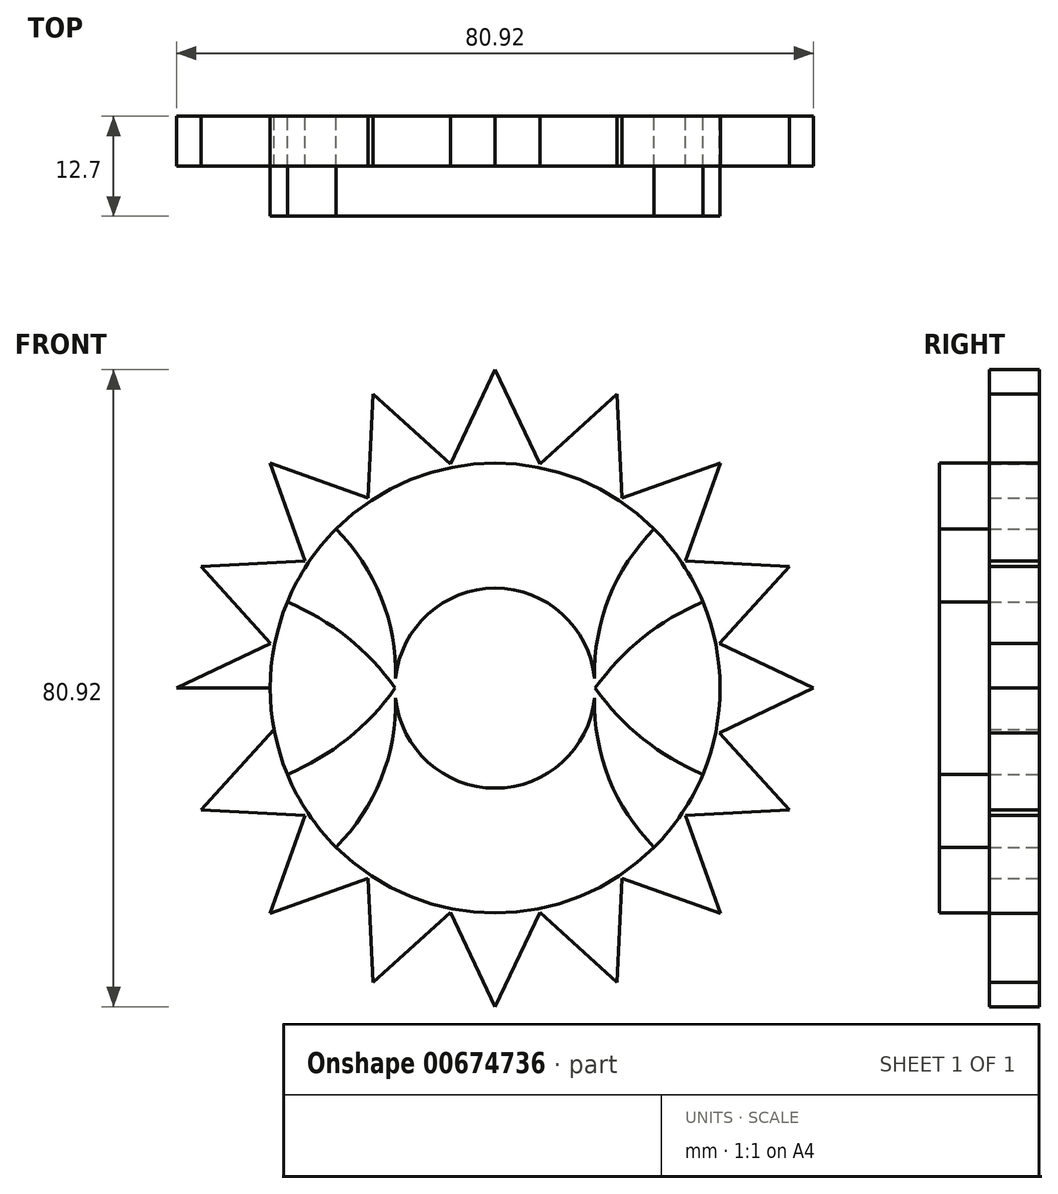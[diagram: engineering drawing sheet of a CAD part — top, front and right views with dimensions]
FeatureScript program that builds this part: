
annotation { "Feature Type Name" : "Feature", "Feature Type Description" : "" }
export const myFeature = defineFeature(function(context is Context, id is Id, definition is map)
    precondition{}
    {
        {
            var Q0;
            Q0=qCreatedBy(makeId("Front.planeOp"),FACE);
            var sketch = newSketch(context, id + "F0", { "sketchPlane" : qUnion([Q0])});
            skCircle(sketch, "E0", {"center": v(0, 0) * mm, "radius": 12.7 * mm});
            skCircle(sketch, "E1", {"center": v(0, 0) * mm, "radius": 28.58 * mm});
            skLineSegment(sketch, "E2", {"start": v(0, 28.58) * mm, "end": v(0, 40.46) * mm});
            skLineSegment(sketch, "E3", {"start": v(0, 40.46) * mm, "end": v(-5.93, 27.95) * mm});
            skLineSegment(sketch, "E4.MirrorCS", {"start": v(0, 40.46) * mm, "end": v(5.93, 27.95) * mm});
            skLineSegment(sketch, "E5.1.0", {"start": v(-15.48, 37.38) * mm, "end": v(-16.17, 23.56) * mm});
            skLineSegment(sketch, "E5.1.1", {"start": v(-15.48, 37.38) * mm, "end": v(-5.22, 28.1) * mm});
            skLineSegment(sketch, "E5.1.2", {"start": v(-10.94, 26.4) * mm, "end": v(-15.48, 37.38) * mm});
            skLineSegment(sketch, "E5.2.0", {"start": v(-28.6, 28.6) * mm, "end": v(-23.96, 15.57) * mm});
            skLineSegment(sketch, "E5.2.1", {"start": v(-28.6, 28.6) * mm, "end": v(-15.57, 23.96) * mm});
            skLineSegment(sketch, "E5.2.2", {"start": v(-20.2, 20.2) * mm, "end": v(-28.6, 28.6) * mm});
            skLineSegment(sketch, "E5.3.0", {"start": v(-37.38, 15.48) * mm, "end": v(-28.1, 5.22) * mm});
            skLineSegment(sketch, "E5.3.1", {"start": v(-37.38, 15.48) * mm, "end": v(-23.56, 16.17) * mm});
            skLineSegment(sketch, "E5.3.2", {"start": v(-26.4, 10.94) * mm, "end": v(-37.38, 15.48) * mm});
            skLineSegment(sketch, "E5.4.0", {"start": v(-40.46, 0) * mm, "end": v(-27.95, -5.93) * mm});
            skLineSegment(sketch, "E5.4.1", {"start": v(-40.46, 0) * mm, "end": v(-27.95, 5.93) * mm});
            skLineSegment(sketch, "E5.4.2", {"start": v(-28.58, 0) * mm, "end": v(-40.46, 0) * mm});
            skLineSegment(sketch, "E5.5.0", {"start": v(-37.38, -15.48) * mm, "end": v(-23.56, -16.17) * mm});
            skLineSegment(sketch, "E5.5.1", {"start": v(-37.38, -15.48) * mm, "end": v(-28.1, -5.22) * mm});
            skLineSegment(sketch, "E5.5.2", {"start": v(-26.4, -10.94) * mm, "end": v(-37.38, -15.48) * mm});
            skLineSegment(sketch, "E5.6.0", {"start": v(-28.6, -28.6) * mm, "end": v(-15.57, -23.96) * mm});
            skLineSegment(sketch, "E5.6.1", {"start": v(-28.6, -28.6) * mm, "end": v(-23.96, -15.57) * mm});
            skLineSegment(sketch, "E5.6.2", {"start": v(-20.2, -20.2) * mm, "end": v(-28.6, -28.6) * mm});
            skLineSegment(sketch, "E5.7.0", {"start": v(-15.48, -37.38) * mm, "end": v(-5.22, -28.1) * mm});
            skLineSegment(sketch, "E5.7.1", {"start": v(-15.48, -37.38) * mm, "end": v(-16.17, -23.56) * mm});
            skLineSegment(sketch, "E5.7.2", {"start": v(-10.94, -26.4) * mm, "end": v(-15.48, -37.38) * mm});
            skLineSegment(sketch, "E5.8.0", {"start": v(0, -40.46) * mm, "end": v(5.93, -27.95) * mm});
            skLineSegment(sketch, "E5.8.1", {"start": v(0, -40.46) * mm, "end": v(-5.93, -27.95) * mm});
            skLineSegment(sketch, "E5.8.2", {"start": v(0, -28.58) * mm, "end": v(0, -40.46) * mm});
            skLineSegment(sketch, "E5.9.0", {"start": v(15.48, -37.38) * mm, "end": v(16.17, -23.56) * mm});
            skLineSegment(sketch, "E5.9.1", {"start": v(15.48, -37.38) * mm, "end": v(5.22, -28.1) * mm});
            skLineSegment(sketch, "E5.9.2", {"start": v(10.94, -26.4) * mm, "end": v(15.48, -37.38) * mm});
            skLineSegment(sketch, "E5.10.0", {"start": v(28.6, -28.6) * mm, "end": v(23.96, -15.57) * mm});
            skLineSegment(sketch, "E5.10.1", {"start": v(28.6, -28.6) * mm, "end": v(15.57, -23.96) * mm});
            skLineSegment(sketch, "E5.10.2", {"start": v(20.2, -20.2) * mm, "end": v(28.6, -28.6) * mm});
            skLineSegment(sketch, "E5.11.0", {"start": v(37.38, -15.48) * mm, "end": v(28.1, -5.22) * mm});
            skLineSegment(sketch, "E5.11.1", {"start": v(37.38, -15.48) * mm, "end": v(23.56, -16.17) * mm});
            skLineSegment(sketch, "E5.11.2", {"start": v(26.4, -10.94) * mm, "end": v(37.38, -15.48) * mm});
            skLineSegment(sketch, "E5.12.0", {"start": v(40.46, 0) * mm, "end": v(27.95, 5.93) * mm});
            skLineSegment(sketch, "E5.12.1", {"start": v(40.46, 0) * mm, "end": v(27.95, -5.93) * mm});
            skLineSegment(sketch, "E5.12.2", {"start": v(28.58, 0) * mm, "end": v(40.46, 0) * mm});
            skLineSegment(sketch, "E5.13.0", {"start": v(37.38, 15.48) * mm, "end": v(23.56, 16.17) * mm});
            skLineSegment(sketch, "E5.13.1", {"start": v(37.38, 15.48) * mm, "end": v(28.1, 5.22) * mm});
            skLineSegment(sketch, "E5.13.2", {"start": v(26.4, 10.94) * mm, "end": v(37.38, 15.48) * mm});
            skLineSegment(sketch, "E5.14.0", {"start": v(28.6, 28.6) * mm, "end": v(15.57, 23.96) * mm});
            skLineSegment(sketch, "E5.14.1", {"start": v(28.6, 28.6) * mm, "end": v(23.96, 15.57) * mm});
            skLineSegment(sketch, "E5.14.2", {"start": v(20.2, 20.2) * mm, "end": v(28.6, 28.6) * mm});
            skLineSegment(sketch, "E5.15.0", {"start": v(15.48, 37.38) * mm, "end": v(5.22, 28.1) * mm});
            skLineSegment(sketch, "E5.15.1", {"start": v(15.48, 37.38) * mm, "end": v(16.17, 23.56) * mm});
            skLineSegment(sketch, "E5.15.2", {"start": v(10.94, 26.4) * mm, "end": v(15.48, 37.38) * mm});
            skLineSegment(sketch, "E6", {"start": v(-28.58, 0) * mm, "end": v(-12.7, 0) * mm});
            skLineSegment(sketch, "E7", {"start": v(0, 28.58) * mm, "end": v(0, 12.7) * mm});
            skLineSegment(sketch, "E8", {"start": v(12.7, 0) * mm, "end": v(28.58, 0) * mm});
            skLineSegment(sketch, "E9", {"start": v(0, -12.7) * mm, "end": v(0, -28.58) * mm});
            skArc(sketch, "E10", {"start": v(-20.2, -20.2) * mm, "mid": v(-14.25, -10.92) * mm, "end": v(-12.7, 0) * mm});
            skArc(sketch, "E11", {"start": v(-26.4, -10.94) * mm, "mid": v(-18.78, -6.44) * mm, "end": v(-12.7, 0) * mm});
            skArc(sketch, "E12.MirrorCS", {"start": v(20.2, -20.2) * mm, "mid": v(14.25, -10.92) * mm, "end": v(12.7, 0) * mm});
            skArc(sketch, "E13.MirrorCS", {"start": v(26.4, -10.94) * mm, "mid": v(18.78, -6.44) * mm, "end": v(12.7, 0) * mm});
            skArc(sketch, "E14.MirrorCS", {"start": v(26.4, 10.94) * mm, "mid": v(18.78, 6.44) * mm, "end": v(12.7, 0) * mm});
            skArc(sketch, "E15.MirrorCS", {"start": v(20.2, 20.2) * mm, "mid": v(14.25, 10.92) * mm, "end": v(12.7, 0) * mm});
            skArc(sketch, "E16.MirrorCS", {"start": v(-26.4, 10.94) * mm, "mid": v(-18.78, 6.44) * mm, "end": v(-12.7, 0) * mm});
            skArc(sketch, "E17.MirrorCS", {"start": v(-20.2, 20.2) * mm, "mid": v(-14.25, 10.92) * mm, "end": v(-12.7, 0) * mm});
            skSolve(sketch);
        }
        {
            var Q0;
            {var subQ0=sQuery(id+"F0.wireOp",EDGE,"E5.12.2");Q0=makeQuery(id+"F0.imprint","IMPRINT",FACE,{"disambiguationData":[TD([[makeQuery(id+"F0.imprint","IMPRINT",EDGE,{"derivedFrom":subQ0}),1.0]])]});}
            var Q1;
            {var subQ0=sQuery(id+"F0.wireOp",EDGE,"E5.12.0");var subQ1=sQuery(id+"F0.wireOp",EDGE,"E1");var subQ2=makeQuery(id+"F0.imprint","INTERSECT",VERTEX,{"derivedFrom":[subQ1,subQ0]});Q1=makeQuery(id+"F0.imprint","IMPRINT",FACE,{"disambiguationData":[TD([[makeQuery(id+"F0.imprint","IMPRINT",EDGE,{"disambiguationData":[TD([[subQ2,1.0]])],"derivedFrom":subQ1}),-1.0]])]});}
            var Q2;
            {var subQ3=sQuery(id+"F0.wireOp",EDGE,"E5.13.2");Q2=makeQuery(id+"F0.imprint","IMPRINT",FACE,{"disambiguationData":[TD([[makeQuery(id+"F0.imprint","IMPRINT",EDGE,{"derivedFrom":subQ3}),-1.0]])]});}
            var Q3;
            {var subQ0=sQuery(id+"F0.wireOp",EDGE,"E5.13.2");Q3=makeQuery(id+"F0.imprint","IMPRINT",FACE,{"disambiguationData":[TD([[makeQuery(id+"F0.imprint","IMPRINT",EDGE,{"derivedFrom":subQ0}),1.0]])]});}
            var Q4;
            {var subQ0=sQuery(id+"F0.wireOp",EDGE,"E5.13.0");var subQ1=sQuery(id+"F0.wireOp",EDGE,"E1");var subQ2=makeQuery(id+"F0.imprint","INTERSECT",VERTEX,{"derivedFrom":[subQ1,subQ0]});Q4=makeQuery(id+"F0.imprint","IMPRINT",FACE,{"disambiguationData":[TD([[makeQuery(id+"F0.imprint","IMPRINT",EDGE,{"disambiguationData":[TD([[subQ2,1.0]])],"derivedFrom":subQ1}),-1.0]])]});}
            var Q5;
            {var subQ3=sQuery(id+"F0.wireOp",EDGE,"E5.14.2");Q5=makeQuery(id+"F0.imprint","IMPRINT",FACE,{"disambiguationData":[TD([[makeQuery(id+"F0.imprint","IMPRINT",EDGE,{"derivedFrom":subQ3}),-1.0]])]});}
            var Q6;
            {var subQ0=sQuery(id+"F0.wireOp",EDGE,"E5.14.2");Q6=makeQuery(id+"F0.imprint","IMPRINT",FACE,{"disambiguationData":[TD([[makeQuery(id+"F0.imprint","IMPRINT",EDGE,{"derivedFrom":subQ0}),1.0]])]});}
            var Q7;
            {var subQ0=sQuery(id+"F0.wireOp",EDGE,"E5.14.0");var subQ1=sQuery(id+"F0.wireOp",EDGE,"E1");var subQ2=makeQuery(id+"F0.imprint","INTERSECT",VERTEX,{"derivedFrom":[subQ1,subQ0]});Q7=makeQuery(id+"F0.imprint","IMPRINT",FACE,{"disambiguationData":[TD([[makeQuery(id+"F0.imprint","IMPRINT",EDGE,{"disambiguationData":[TD([[subQ2,1.0]])],"derivedFrom":subQ1}),-1.0]])]});}
            var Q8;
            {var subQ3=sQuery(id+"F0.wireOp",EDGE,"E5.15.2");Q8=makeQuery(id+"F0.imprint","IMPRINT",FACE,{"disambiguationData":[TD([[makeQuery(id+"F0.imprint","IMPRINT",EDGE,{"derivedFrom":subQ3}),-1.0]])]});}
            var Q9;
            {var subQ3=sQuery(id+"F0.wireOp",EDGE,"E5.15.2");Q9=makeQuery(id+"F0.imprint","IMPRINT",FACE,{"disambiguationData":[TD([[makeQuery(id+"F0.imprint","IMPRINT",EDGE,{"derivedFrom":subQ3}),1.0]])]});}
            var Q10;
            {var subQ0=sQuery(id+"F0.wireOp",EDGE,"E4.MirrorCS");var subQ1=sQuery(id+"F0.wireOp",EDGE,"E1");var subQ2=makeQuery(id+"F0.imprint","INTERSECT",VERTEX,{"derivedFrom":[subQ1,subQ0]});Q10=makeQuery(id+"F0.imprint","IMPRINT",FACE,{"disambiguationData":[TD([[makeQuery(id+"F0.imprint","IMPRINT",EDGE,{"disambiguationData":[TD([[subQ2,-1.0]])],"derivedFrom":subQ1}),-1.0]])]});}
            var Q11;
            {var subQ0=sQuery(id+"F0.wireOp",EDGE,"E2");Q11=makeQuery(id+"F0.imprint","IMPRINT",FACE,{"disambiguationData":[TD([[makeQuery(id+"F0.imprint","IMPRINT",EDGE,{"derivedFrom":subQ0}),-1.0]])]});}
            var Q12;
            {var subQ0=sQuery(id+"F0.wireOp",EDGE,"E2");Q12=makeQuery(id+"F0.imprint","IMPRINT",FACE,{"disambiguationData":[TD([[makeQuery(id+"F0.imprint","IMPRINT",EDGE,{"derivedFrom":subQ0}),1.0]])]});}
            var Q13;
            {var subQ0=sQuery(id+"F0.wireOp",EDGE,"E3");var subQ1=sQuery(id+"F0.wireOp",EDGE,"E1");var subQ2=makeQuery(id+"F0.imprint","INTERSECT",VERTEX,{"derivedFrom":[subQ1,subQ0]});Q13=makeQuery(id+"F0.imprint","IMPRINT",FACE,{"disambiguationData":[TD([[makeQuery(id+"F0.imprint","IMPRINT",EDGE,{"disambiguationData":[TD([[subQ2,1.0]])],"derivedFrom":subQ1}),-1.0]])]});}
            var Q14;
            {var subQ3=sQuery(id+"F0.wireOp",EDGE,"E5.1.2");Q14=makeQuery(id+"F0.imprint","IMPRINT",FACE,{"disambiguationData":[TD([[makeQuery(id+"F0.imprint","IMPRINT",EDGE,{"derivedFrom":subQ3}),-1.0]])]});}
            var Q15;
            {var subQ0=sQuery(id+"F0.wireOp",EDGE,"E5.1.2");Q15=makeQuery(id+"F0.imprint","IMPRINT",FACE,{"disambiguationData":[TD([[makeQuery(id+"F0.imprint","IMPRINT",EDGE,{"derivedFrom":subQ0}),1.0]])]});}
            var Q16;
            {var subQ0=sQuery(id+"F0.wireOp",EDGE,"E5.1.0");var subQ1=sQuery(id+"F0.wireOp",EDGE,"E1");var subQ2=makeQuery(id+"F0.imprint","INTERSECT",VERTEX,{"derivedFrom":[subQ1,subQ0]});Q16=makeQuery(id+"F0.imprint","IMPRINT",FACE,{"disambiguationData":[TD([[makeQuery(id+"F0.imprint","IMPRINT",EDGE,{"disambiguationData":[TD([[subQ2,1.0]])],"derivedFrom":subQ1}),-1.0]])]});}
            var Q17;
            {var subQ3=sQuery(id+"F0.wireOp",EDGE,"E5.2.2");Q17=makeQuery(id+"F0.imprint","IMPRINT",FACE,{"disambiguationData":[TD([[makeQuery(id+"F0.imprint","IMPRINT",EDGE,{"derivedFrom":subQ3}),-1.0]])]});}
            var Q18;
            {var subQ0=sQuery(id+"F0.wireOp",EDGE,"E5.2.2");Q18=makeQuery(id+"F0.imprint","IMPRINT",FACE,{"disambiguationData":[TD([[makeQuery(id+"F0.imprint","IMPRINT",EDGE,{"derivedFrom":subQ0}),1.0]])]});}
            var Q19;
            {var subQ0=sQuery(id+"F0.wireOp",EDGE,"E5.2.0");var subQ1=sQuery(id+"F0.wireOp",EDGE,"E1");var subQ2=makeQuery(id+"F0.imprint","INTERSECT",VERTEX,{"derivedFrom":[subQ1,subQ0]});Q19=makeQuery(id+"F0.imprint","IMPRINT",FACE,{"disambiguationData":[TD([[makeQuery(id+"F0.imprint","IMPRINT",EDGE,{"disambiguationData":[TD([[subQ2,1.0]])],"derivedFrom":subQ1}),-1.0]])]});}
            var Q20;
            {var subQ3=sQuery(id+"F0.wireOp",EDGE,"E5.3.2");Q20=makeQuery(id+"F0.imprint","IMPRINT",FACE,{"disambiguationData":[TD([[makeQuery(id+"F0.imprint","IMPRINT",EDGE,{"derivedFrom":subQ3}),-1.0]])]});}
            var Q21;
            {var subQ0=sQuery(id+"F0.wireOp",EDGE,"E5.3.2");Q21=makeQuery(id+"F0.imprint","IMPRINT",FACE,{"disambiguationData":[TD([[makeQuery(id+"F0.imprint","IMPRINT",EDGE,{"derivedFrom":subQ0}),1.0]])]});}
            var Q22;
            {var subQ0=sQuery(id+"F0.wireOp",EDGE,"E5.3.0");var subQ1=sQuery(id+"F0.wireOp",EDGE,"E1");var subQ2=makeQuery(id+"F0.imprint","INTERSECT",VERTEX,{"derivedFrom":[subQ1,subQ0]});Q22=makeQuery(id+"F0.imprint","IMPRINT",FACE,{"disambiguationData":[TD([[makeQuery(id+"F0.imprint","IMPRINT",EDGE,{"disambiguationData":[TD([[subQ2,1.0]])],"derivedFrom":subQ1}),-1.0]])]});}
            var Q23;
            {var subQ3=sQuery(id+"F0.wireOp",EDGE,"E5.4.2");Q23=makeQuery(id+"F0.imprint","IMPRINT",FACE,{"disambiguationData":[TD([[makeQuery(id+"F0.imprint","IMPRINT",EDGE,{"derivedFrom":subQ3}),-1.0]])]});}
            var Q24;
            {var subQ0=sQuery(id+"F0.wireOp",EDGE,"E5.4.0");var subQ1=sQuery(id+"F0.wireOp",EDGE,"E1");var subQ2=makeQuery(id+"F0.imprint","INTERSECT",VERTEX,{"derivedFrom":[subQ1,subQ0]});Q24=makeQuery(id+"F0.imprint","IMPRINT",FACE,{"disambiguationData":[TD([[makeQuery(id+"F0.imprint","IMPRINT",EDGE,{"disambiguationData":[TD([[subQ2,1.0]])],"derivedFrom":subQ1}),-1.0]])]});}
            var Q25;
            {var subQ3=sQuery(id+"F0.wireOp",EDGE,"E5.5.2");Q25=makeQuery(id+"F0.imprint","IMPRINT",FACE,{"disambiguationData":[TD([[makeQuery(id+"F0.imprint","IMPRINT",EDGE,{"derivedFrom":subQ3}),-1.0]])]});}
            var Q26;
            {var subQ0=sQuery(id+"F0.wireOp",EDGE,"E5.5.2");Q26=makeQuery(id+"F0.imprint","IMPRINT",FACE,{"disambiguationData":[TD([[makeQuery(id+"F0.imprint","IMPRINT",EDGE,{"derivedFrom":subQ0}),1.0]])]});}
            var Q27;
            {var subQ0=sQuery(id+"F0.wireOp",EDGE,"E5.5.0");var subQ1=sQuery(id+"F0.wireOp",EDGE,"E1");var subQ2=makeQuery(id+"F0.imprint","INTERSECT",VERTEX,{"derivedFrom":[subQ1,subQ0]});Q27=makeQuery(id+"F0.imprint","IMPRINT",FACE,{"disambiguationData":[TD([[makeQuery(id+"F0.imprint","IMPRINT",EDGE,{"disambiguationData":[TD([[subQ2,1.0]])],"derivedFrom":subQ1}),-1.0]])]});}
            var Q28;
            {var subQ3=sQuery(id+"F0.wireOp",EDGE,"E5.6.2");Q28=makeQuery(id+"F0.imprint","IMPRINT",FACE,{"disambiguationData":[TD([[makeQuery(id+"F0.imprint","IMPRINT",EDGE,{"derivedFrom":subQ3}),-1.0]])]});}
            var Q29;
            {var subQ0=sQuery(id+"F0.wireOp",EDGE,"E5.6.2");Q29=makeQuery(id+"F0.imprint","IMPRINT",FACE,{"disambiguationData":[TD([[makeQuery(id+"F0.imprint","IMPRINT",EDGE,{"derivedFrom":subQ0}),1.0]])]});}
            var Q30;
            {var subQ0=sQuery(id+"F0.wireOp",EDGE,"E5.6.0");var subQ1=sQuery(id+"F0.wireOp",EDGE,"E1");var subQ2=makeQuery(id+"F0.imprint","INTERSECT",VERTEX,{"derivedFrom":[subQ1,subQ0]});Q30=makeQuery(id+"F0.imprint","IMPRINT",FACE,{"disambiguationData":[TD([[makeQuery(id+"F0.imprint","IMPRINT",EDGE,{"disambiguationData":[TD([[subQ2,1.0]])],"derivedFrom":subQ1}),-1.0]])]});}
            var Q31;
            {var subQ3=sQuery(id+"F0.wireOp",EDGE,"E5.7.2");Q31=makeQuery(id+"F0.imprint","IMPRINT",FACE,{"disambiguationData":[TD([[makeQuery(id+"F0.imprint","IMPRINT",EDGE,{"derivedFrom":subQ3}),-1.0]])]});}
            var Q32;
            {var subQ0=sQuery(id+"F0.wireOp",EDGE,"E5.7.2");Q32=makeQuery(id+"F0.imprint","IMPRINT",FACE,{"disambiguationData":[TD([[makeQuery(id+"F0.imprint","IMPRINT",EDGE,{"derivedFrom":subQ0}),1.0]])]});}
            var Q33;
            {var subQ0=sQuery(id+"F0.wireOp",EDGE,"E5.7.0");var subQ1=sQuery(id+"F0.wireOp",EDGE,"E1");var subQ2=makeQuery(id+"F0.imprint","INTERSECT",VERTEX,{"derivedFrom":[subQ1,subQ0]});Q33=makeQuery(id+"F0.imprint","IMPRINT",FACE,{"disambiguationData":[TD([[makeQuery(id+"F0.imprint","IMPRINT",EDGE,{"disambiguationData":[TD([[subQ2,1.0]])],"derivedFrom":subQ1}),-1.0]])]});}
            var Q34;
            {var subQ3=sQuery(id+"F0.wireOp",EDGE,"E5.8.2");Q34=makeQuery(id+"F0.imprint","IMPRINT",FACE,{"disambiguationData":[TD([[makeQuery(id+"F0.imprint","IMPRINT",EDGE,{"derivedFrom":subQ3}),-1.0]])]});}
            var Q35;
            {var subQ0=sQuery(id+"F0.wireOp",EDGE,"E5.8.2");Q35=makeQuery(id+"F0.imprint","IMPRINT",FACE,{"disambiguationData":[TD([[makeQuery(id+"F0.imprint","IMPRINT",EDGE,{"derivedFrom":subQ0}),1.0]])]});}
            var Q36;
            {var subQ0=sQuery(id+"F0.wireOp",EDGE,"E5.8.0");var subQ1=sQuery(id+"F0.wireOp",EDGE,"E1");var subQ2=makeQuery(id+"F0.imprint","INTERSECT",VERTEX,{"derivedFrom":[subQ1,subQ0]});Q36=makeQuery(id+"F0.imprint","IMPRINT",FACE,{"disambiguationData":[TD([[makeQuery(id+"F0.imprint","IMPRINT",EDGE,{"disambiguationData":[TD([[subQ2,1.0]])],"derivedFrom":subQ1}),-1.0]])]});}
            var Q37;
            {var subQ3=sQuery(id+"F0.wireOp",EDGE,"E5.9.2");Q37=makeQuery(id+"F0.imprint","IMPRINT",FACE,{"disambiguationData":[TD([[makeQuery(id+"F0.imprint","IMPRINT",EDGE,{"derivedFrom":subQ3}),-1.0]])]});}
            var Q38;
            {var subQ0=sQuery(id+"F0.wireOp",EDGE,"E5.9.2");Q38=makeQuery(id+"F0.imprint","IMPRINT",FACE,{"disambiguationData":[TD([[makeQuery(id+"F0.imprint","IMPRINT",EDGE,{"derivedFrom":subQ0}),1.0]])]});}
            var Q39;
            {var subQ0=sQuery(id+"F0.wireOp",EDGE,"E5.9.0");var subQ1=sQuery(id+"F0.wireOp",EDGE,"E1");var subQ2=makeQuery(id+"F0.imprint","INTERSECT",VERTEX,{"derivedFrom":[subQ1,subQ0]});Q39=makeQuery(id+"F0.imprint","IMPRINT",FACE,{"disambiguationData":[TD([[makeQuery(id+"F0.imprint","IMPRINT",EDGE,{"disambiguationData":[TD([[subQ2,1.0]])],"derivedFrom":subQ1}),-1.0]])]});}
            var Q40;
            {var subQ3=sQuery(id+"F0.wireOp",EDGE,"E5.10.2");Q40=makeQuery(id+"F0.imprint","IMPRINT",FACE,{"disambiguationData":[TD([[makeQuery(id+"F0.imprint","IMPRINT",EDGE,{"derivedFrom":subQ3}),-1.0]])]});}
            var Q41;
            {var subQ0=sQuery(id+"F0.wireOp",EDGE,"E5.10.2");Q41=makeQuery(id+"F0.imprint","IMPRINT",FACE,{"disambiguationData":[TD([[makeQuery(id+"F0.imprint","IMPRINT",EDGE,{"derivedFrom":subQ0}),1.0]])]});}
            var Q42;
            {var subQ0=sQuery(id+"F0.wireOp",EDGE,"E5.10.0");var subQ1=sQuery(id+"F0.wireOp",EDGE,"E1");var subQ2=makeQuery(id+"F0.imprint","INTERSECT",VERTEX,{"derivedFrom":[subQ1,subQ0]});Q42=makeQuery(id+"F0.imprint","IMPRINT",FACE,{"disambiguationData":[TD([[makeQuery(id+"F0.imprint","IMPRINT",EDGE,{"disambiguationData":[TD([[subQ2,1.0]])],"derivedFrom":subQ1}),-1.0]])]});}
            var Q43;
            {var subQ3=sQuery(id+"F0.wireOp",EDGE,"E5.11.2");Q43=makeQuery(id+"F0.imprint","IMPRINT",FACE,{"disambiguationData":[TD([[makeQuery(id+"F0.imprint","IMPRINT",EDGE,{"derivedFrom":subQ3}),-1.0]])]});}
            var Q44;
            {var subQ0=sQuery(id+"F0.wireOp",EDGE,"E5.11.2");Q44=makeQuery(id+"F0.imprint","IMPRINT",FACE,{"disambiguationData":[TD([[makeQuery(id+"F0.imprint","IMPRINT",EDGE,{"derivedFrom":subQ0}),1.0]])]});}
            var Q45;
            {var subQ0=sQuery(id+"F0.wireOp",EDGE,"E5.11.0");var subQ1=sQuery(id+"F0.wireOp",EDGE,"E1");var subQ2=makeQuery(id+"F0.imprint","INTERSECT",VERTEX,{"derivedFrom":[subQ1,subQ0]});Q45=makeQuery(id+"F0.imprint","IMPRINT",FACE,{"disambiguationData":[TD([[makeQuery(id+"F0.imprint","IMPRINT",EDGE,{"disambiguationData":[TD([[subQ2,1.0]])],"derivedFrom":subQ1}),-1.0]])]});}
            var Q46;
            {var subQ3=sQuery(id+"F0.wireOp",EDGE,"E5.12.2");Q46=makeQuery(id+"F0.imprint","IMPRINT",FACE,{"disambiguationData":[TD([[makeQuery(id+"F0.imprint","IMPRINT",EDGE,{"derivedFrom":subQ3}),-1.0]])]});}
            extrude(context, id + "F1", {"entities" : qUnion([Q0, Q1, Q2, Q3, Q4, Q5, Q6, Q7, Q8, Q9, Q10, Q11, Q12, Q13, Q14, Q15, Q16, Q17, Q18, Q19, Q20, Q21, Q22, Q23, Q24, Q25, Q26, Q27, Q28, Q29, Q30, Q31, Q32, Q33, Q34, Q35, Q36, Q37, Q38, Q39, Q40, Q41, Q42, Q43, Q44, Q45, Q46]), "depth" : 6.35 * mm, "offsetDistance" : 25.4 * mm});
        }
        {
            var Q0;
            {var subQ3=sQuery(id+"F0.wireOp",EDGE,"E7");Q0=makeQuery(id+"F0.imprint","IMPRINT",FACE,{"disambiguationData":[TD([[makeQuery(id+"F0.imprint","IMPRINT",EDGE,{"derivedFrom":subQ3}),-1.0]])]});}
            var Q1;
            {var subQ8=sQuery(id+"F0.wireOp",EDGE,"E7");Q1=makeQuery(id+"F0.imprint","IMPRINT",FACE,{"disambiguationData":[TD([[makeQuery(id+"F0.imprint","IMPRINT",EDGE,{"derivedFrom":subQ8}),1.0]])]});}
            var Q2;
            {var subQ0=sQuery(id+"F0.wireOp",EDGE,"E6");Q2=makeQuery(id+"F0.imprint","IMPRINT",FACE,{"disambiguationData":[TD([[makeQuery(id+"F0.imprint","IMPRINT",EDGE,{"derivedFrom":subQ0}),1.0]])]});}
            var Q3;
            {var subQ0=sQuery(id+"F0.wireOp",EDGE,"E6");Q3=makeQuery(id+"F0.imprint","IMPRINT",FACE,{"disambiguationData":[TD([[makeQuery(id+"F0.imprint","IMPRINT",EDGE,{"derivedFrom":subQ0}),-1.0]])]});}
            var Q4;
            {var subQ5=sQuery(id+"F0.wireOp",EDGE,"E9");Q4=makeQuery(id+"F0.imprint","IMPRINT",FACE,{"disambiguationData":[TD([[makeQuery(id+"F0.imprint","IMPRINT",EDGE,{"derivedFrom":subQ5}),-1.0]])]});}
            var Q5;
            {var subQ3=sQuery(id+"F0.wireOp",EDGE,"E9");Q5=makeQuery(id+"F0.imprint","IMPRINT",FACE,{"disambiguationData":[TD([[makeQuery(id+"F0.imprint","IMPRINT",EDGE,{"derivedFrom":subQ3}),1.0]])]});}
            var Q6;
            {var subQ4=sQuery(id+"F0.wireOp",EDGE,"E8");Q6=makeQuery(id+"F0.imprint","IMPRINT",FACE,{"disambiguationData":[TD([[makeQuery(id+"F0.imprint","IMPRINT",EDGE,{"derivedFrom":subQ4}),1.0]])]});}
            var Q7;
            {var subQ2=sQuery(id+"F0.wireOp",EDGE,"E8");Q7=makeQuery(id+"F0.imprint","IMPRINT",FACE,{"disambiguationData":[TD([[makeQuery(id+"F0.imprint","IMPRINT",EDGE,{"derivedFrom":subQ2}),-1.0]])]});}
            extrude(context, id + "F2", {"entities" : qUnion([Q0, Q1, Q2, Q3, Q4, Q5, Q6, Q7]), "operationType" : NewBodyOperationType.ADD, "depth" : 12.7 * mm, "offsetDistance" : 25.4 * mm});
        }
    });
